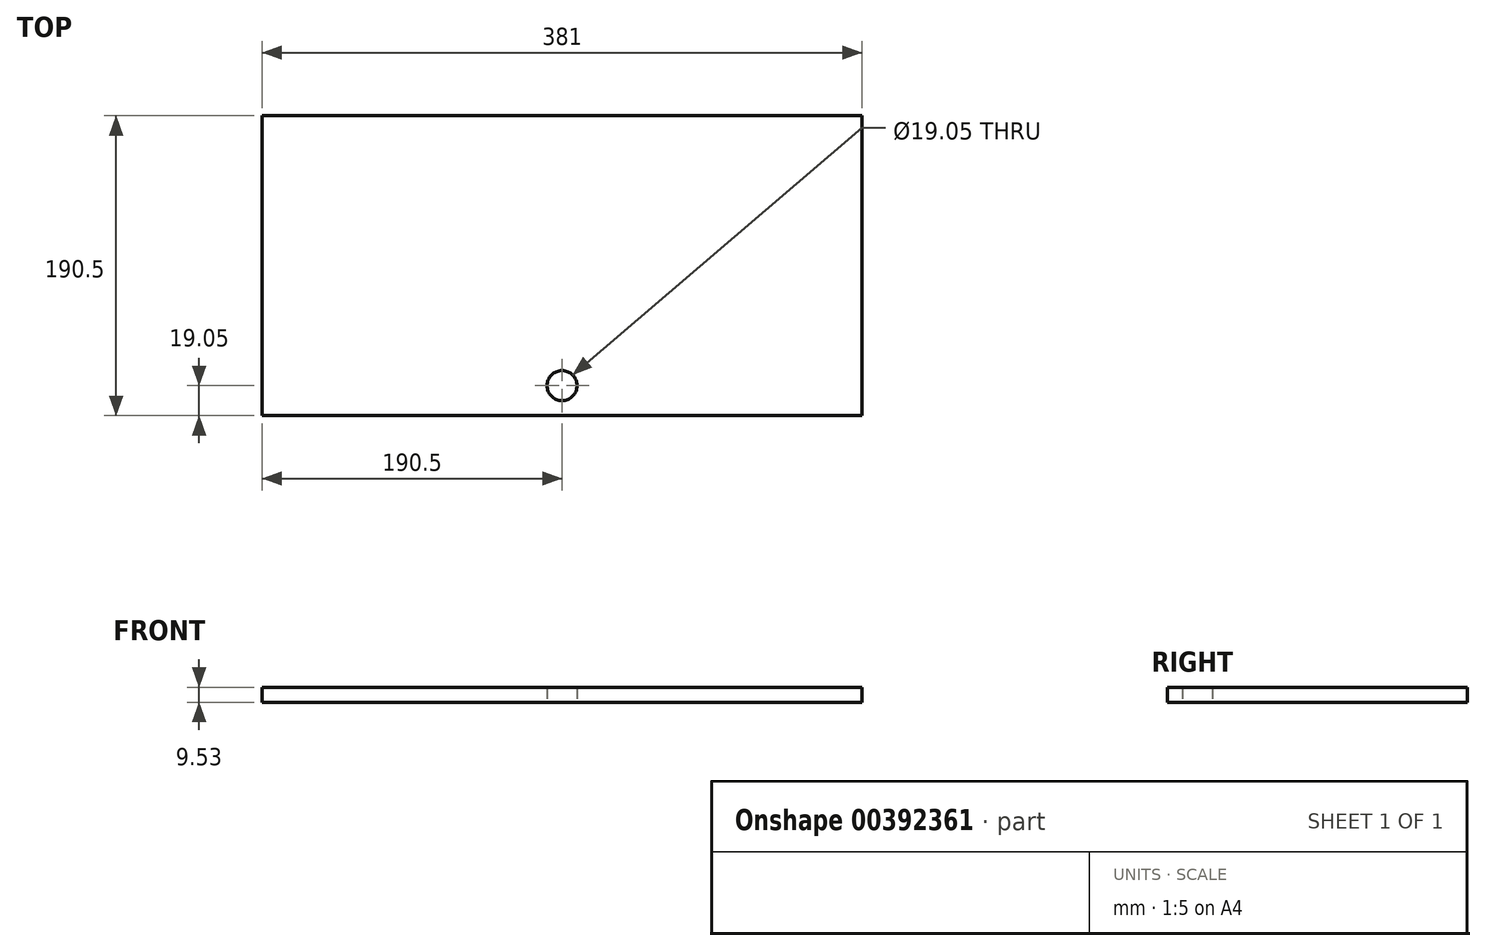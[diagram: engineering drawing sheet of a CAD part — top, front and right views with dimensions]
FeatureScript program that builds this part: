
annotation { "Feature Type Name" : "Feature", "Feature Type Description" : "" }
export const myFeature = defineFeature(function(context is Context, id is Id, definition is map)
    precondition{}
    {
        {
            var Q0;
            Q0=qCreatedBy(makeId("Top.planeOp"),FACE);
            var sketch = newSketch(context, id + "F0", { "sketchPlane" : qUnion([Q0])});
            skLineSegment(sketch, "E0.bottom", {"start": v(-190.5, 0) * mm, "end": v(190.5, 0) * mm});
            skLineSegment(sketch, "E0.top", {"start": v(-190.5, -190.5) * mm, "end": v(190.5, -190.5) * mm});
            skLineSegment(sketch, "E0.left", {"start": v(-190.5, 0) * mm, "end": v(-190.5, -190.5) * mm});
            skLineSegment(sketch, "E0.right", {"start": v(190.5, 0) * mm, "end": v(190.5, -190.5) * mm});
            skCircle(sketch, "E1", {"center": v(0, -171.45) * mm, "radius": 9.53 * mm});
            skSolve(sketch);
        }
        {
            var Q0;
            Q0=makeQuery(id+"F0.imprint","IMPRINT",FACE,{"disambiguationData":[TD([[makeQuery(id+"F0.imprint","IMPRINT",EDGE,{"derivedFrom":sQuery(id+"F0.wireOp",EDGE,"E0.bottom")}),-1.0]])]});
            extrude(context, id + "F1", {"entities" : qUnion([Q0]), "depth" : 9.52 * mm});
        }
    });
